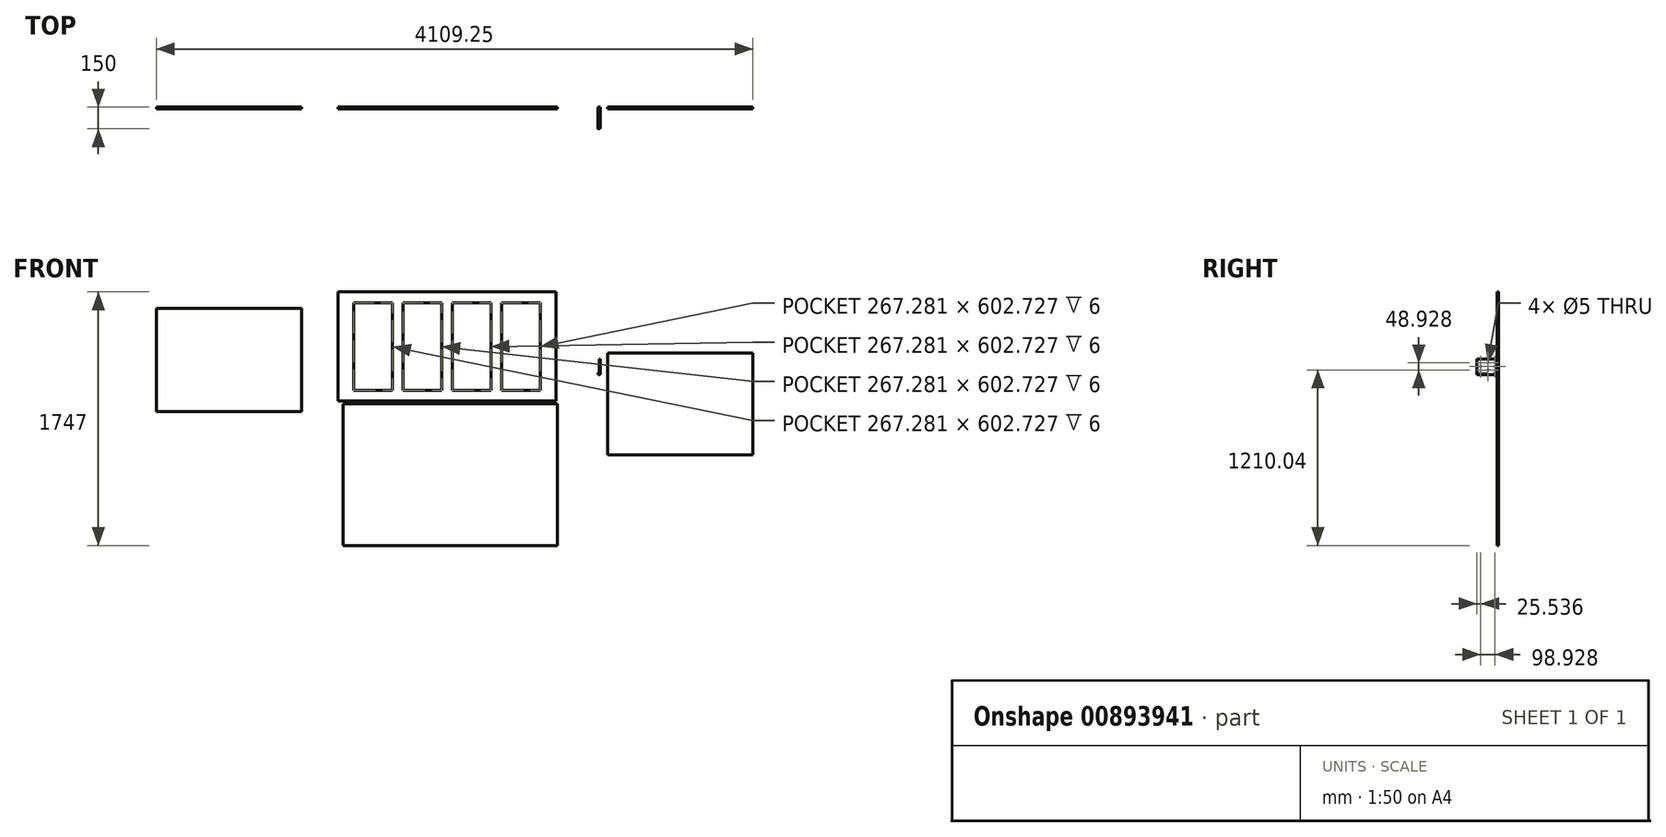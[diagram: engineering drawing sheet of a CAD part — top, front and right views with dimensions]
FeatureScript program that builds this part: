
annotation { "Feature Type Name" : "Feature", "Feature Type Description" : "" }
export const myFeature = defineFeature(function(context is Context, id is Id, definition is map)
    precondition{}
    {
        {
            assignVariable(context, id + "F0", {"name" : "thickness", "anyValue" : 12 * mm});
        }
        {
            var Q0;
            Q0=qCreatedBy(makeId("Front.planeOp"),FACE);
            var sketch = newSketch(context, id + "F1", { "sketchPlane" : qUnion([Q0])});
            skLineSegment(sketch, "E0.bottom", {"start": v(-755.12, 365.58) * mm, "end": v(744.88, 365.58) * mm});
            skLineSegment(sketch, "E0.top", {"start": v(-755.12, -384.42) * mm, "end": v(744.88, -384.42) * mm});
            skLineSegment(sketch, "E0.left", {"start": v(-755.12, 365.58) * mm, "end": v(-755.12, -384.42) * mm});
            skLineSegment(sketch, "E0.right", {"start": v(744.88, 365.58) * mm, "end": v(744.88, -384.42) * mm});
            skSolve(sketch);
        }
        {
            var Q0;
            Q0=makeQuery(id+"F1.imprint","IMPRINT",FACE,{"disambiguationData":[TD([[makeQuery(id+"F1.imprint","IMPRINT",EDGE,{"derivedFrom":sQuery(id+"F1.wireOp",EDGE,"E0.bottom")}),-1.0]])]});
            extrude(context, id + "F2", {"entities" : qUnion([Q0]), "depth" : getVariable(context, 'thickness'), "offsetDistance" : 25 * mm});
        }
        {
            var Q0;
            Q0=makeQuery(id+"F2.opExtrude","CAP_FACE",FACE,{"disambiguationData":[OSD([sQuery(id+"F1.wireOp",EDGE,"E0.bottom"),sQuery(id+"F1.wireOp",EDGE,"E0.top"),sQuery(id+"F1.wireOp",EDGE,"E0.left"),sQuery(id+"F1.wireOp",EDGE,"E0.right")])],"isStart":false});
            var sketch = newSketch(context, id + "F3", { "sketchPlane" : qUnion([Q0])});
            skLineSegment(sketch, "E1.bottom", {"start": v(-647.31, 291.94) * mm, "end": v(-380.03, 291.94) * mm});
            skLineSegment(sketch, "E1.top", {"start": v(-647.31, -310.78) * mm, "end": v(-380.03, -310.78) * mm});
            skLineSegment(sketch, "E1.left", {"start": v(-647.31, 291.94) * mm, "end": v(-647.31, -310.78) * mm});
            skLineSegment(sketch, "E1.right", {"start": v(-380.03, 291.94) * mm, "end": v(-380.03, -310.78) * mm});
            skLineSegment(sketch, "E2.bottom", {"start": v(-308.27, 291.94) * mm, "end": v(-41, 291.94) * mm});
            skLineSegment(sketch, "E2.top", {"start": v(-308.27, -310.78) * mm, "end": v(-41, -310.78) * mm});
            skLineSegment(sketch, "E2.left", {"start": v(-308.27, 291.94) * mm, "end": v(-308.27, -310.78) * mm});
            skLineSegment(sketch, "E2.right", {"start": v(-41, 291.94) * mm, "end": v(-41, -310.78) * mm});
            skLineSegment(sketch, "E3.bottom", {"start": v(30.76, -310.78) * mm, "end": v(298.04, -310.78) * mm});
            skLineSegment(sketch, "E3.top", {"start": v(30.76, 291.94) * mm, "end": v(298.04, 291.94) * mm});
            skLineSegment(sketch, "E3.left", {"start": v(30.76, -310.78) * mm, "end": v(30.76, 291.94) * mm});
            skLineSegment(sketch, "E3.right", {"start": v(298.04, -310.78) * mm, "end": v(298.04, 291.94) * mm});
            skLineSegment(sketch, "E4.bottom", {"start": v(369.8, -310.78) * mm, "end": v(637.08, -310.78) * mm});
            skLineSegment(sketch, "E4.top", {"start": v(369.8, 291.94) * mm, "end": v(637.08, 291.94) * mm});
            skLineSegment(sketch, "E4.left", {"start": v(369.8, -310.78) * mm, "end": v(369.8, 291.94) * mm});
            skLineSegment(sketch, "E4.right", {"start": v(637.08, -310.78) * mm, "end": v(637.08, 291.94) * mm});
            skLineSegment(sketch, "E5", {"start": v(-308.27, 291.94) * mm, "end": v(-308.27, 365.58) * mm, "construction": true});
            skLineSegment(sketch, "E6", {"start": v(-308.27, -310.78) * mm, "end": v(-308.27, -384.42) * mm, "construction": true});
            skLineSegment(sketch, "E7", {"start": v(-380.03, 291.94) * mm, "end": v(-380.03, 365.58) * mm, "construction": true});
            skLineSegment(sketch, "E8", {"start": v(-10.67, 291.94) * mm, "end": v(-10.67, 365.58) * mm, "construction": true});
            skLineSegment(sketch, "E9", {"start": v(369.8, 291.94) * mm, "end": v(369.8, 365.58) * mm, "construction": true});
            skLineSegment(sketch, "E10", {"start": v(-380.03, -310.78) * mm, "end": v(-380.03, -384.42) * mm, "construction": true});
            skLineSegment(sketch, "E11", {"start": v(30.76, -310.78) * mm, "end": v(30.76, -384.42) * mm, "construction": true});
            skLineSegment(sketch, "E12", {"start": v(369.8, -384.42) * mm, "end": v(369.8, -310.78) * mm, "construction": true});
            skLineSegment(sketch, "E13", {"start": v(-380.03, 291.94) * mm, "end": v(-308.27, 291.94) * mm, "construction": true});
            skLineSegment(sketch, "E14", {"start": v(-41, 291.94) * mm, "end": v(30.76, 291.94) * mm, "construction": true});
            skLineSegment(sketch, "E15", {"start": v(298.04, 291.94) * mm, "end": v(369.8, 291.94) * mm, "construction": true});
            skLineSegment(sketch, "E16", {"start": v(-647.31, 291.94) * mm, "end": v(-755.12, 291.94) * mm, "construction": true});
            skLineSegment(sketch, "E17", {"start": v(637.08, 291.94) * mm, "end": v(744.88, 291.94) * mm, "construction": true});
            skSolve(sketch);
        }
        {
            var Q0;
            Q0=makeQuery(id+"F3.imprint","IMPRINT",FACE,{"disambiguationData":[TD([[makeQuery(id+"F3.imprint","IMPRINT",EDGE,{"derivedFrom":sQuery(id+"F3.wireOp",EDGE,"E1.bottom")}),-1.0]])]});
            var Q1;
            Q1=makeQuery(id+"F3.imprint","IMPRINT",FACE,{"disambiguationData":[TD([[makeQuery(id+"F3.imprint","IMPRINT",EDGE,{"derivedFrom":sQuery(id+"F3.wireOp",EDGE,"E2.bottom")}),-1.0]])]});
            var Q2;
            Q2=makeQuery(id+"F3.imprint","IMPRINT",FACE,{"disambiguationData":[TD([[makeQuery(id+"F3.imprint","IMPRINT",EDGE,{"derivedFrom":sQuery(id+"F3.wireOp",EDGE,"E3.bottom")}),1.0]])]});
            var Q3;
            Q3=makeQuery(id+"F3.imprint","IMPRINT",FACE,{"disambiguationData":[TD([[makeQuery(id+"F3.imprint","IMPRINT",EDGE,{"derivedFrom":sQuery(id+"F3.wireOp",EDGE,"E4.bottom")}),1.0]])]});
            extrude(context, id + "F4", {"entities" : qUnion([Q0, Q1, Q2, Q3]), "operationType" : NewBodyOperationType.REMOVE, "oppositeDirection" : true, "depth" : getVariable(context, 'thickness') / 2, "offsetDistance" : 25 * mm});
        }
        {
            var Q0;
            Q0=qCreatedBy(makeId("Front.planeOp"),FACE);
            var sketch = newSketch(context, id + "F5", { "sketchPlane" : qUnion([Q0])});
            skCircle(sketch, "E18", {"center": v(1043.1, -196.91) * mm, "radius": 7.5 * mm});
            skLineSegment(sketch, "E19", {"start": v(1045.6, -189.84) * mm, "end": v(1045.6, -96.91) * mm});
            skLineSegment(sketch, "E20", {"start": v(1045.6, -96.91) * mm, "end": v(1050.6, -96.91) * mm});
            skLineSegment(sketch, "E21", {"start": v(1050.6, -96.91) * mm, "end": v(1050.6, -196.91) * mm});
            skPoint(sketch, "E22", {"position": v(1048.1, -96.91) * mm});
            skSolve(sketch);
        }
        {
            var Q0;
            {var subQ0=sQuery(id+"F5.wireOp",EDGE,"E19");Q0=makeQuery(id+"F5.imprint","IMPRINT",FACE,{"disambiguationData":[TD([[makeQuery(id+"F5.imprint","IMPRINT",EDGE,{"derivedFrom":subQ0}),-1.0]])]});}
            var Q1;
            {var subQ0=sQuery(id+"F5.wireOp",EDGE,"E18");var subQ1=makeQuery(id+"F5.imprint","INTERSECT",VERTEX,{"derivedFrom":[subQ0,sQuery(id+"F5.wireOp",EDGE,"E19")]});Q1=makeQuery(id+"F5.imprint","IMPRINT",FACE,{"disambiguationData":[TD([[makeQuery(id+"F5.imprint","IMPRINT",EDGE,{"disambiguationData":[TD([[subQ1,1.0]])],"derivedFrom":subQ0}),1.0]])]});}
            extrude(context, id + "F6", {"entities" : qUnion([Q0, Q1]), "depth" : 150 * mm, "offsetDistance" : 25 * mm});
        }
        {
            var Q0;
            Q0=makeQuery(id+"F6.opExtrude","SWEPT_FACE",FACE,{"disambiguationData":[OSD([sQuery(id+"F5.wireOp",EDGE,"E21")])]});
            var sketch = newSketch(context, id + "F7", { "sketchPlane" : qUnion([Q0])});
            skPoint(sketch, "E23", {"position": v(-150, -146.91) * mm});
            skPoint(sketch, "E24", {"position": v(0, -146.91) * mm});
            skCircle(sketch, "E25", {"center": v(-124.46, -146.91) * mm, "radius": 2.5 * mm});
            skCircle(sketch, "E26", {"center": v(-25.54, -146.91) * mm, "radius": 2.5 * mm});
            skCircle(sketch, "E27", {"center": v(-75, -122.45) * mm, "radius": 2.5 * mm});
            skCircle(sketch, "E28", {"center": v(-75, -171.38) * mm, "radius": 2.5 * mm});
            skPoint(sketch, "E29", {"position": v(-75, -96.91) * mm});
            skLineSegment(sketch, "E30", {"start": v(-124.46, -146.91) * mm, "end": v(-150, -146.91) * mm, "construction": true});
            skLineSegment(sketch, "E31", {"start": v(-75, -122.45) * mm, "end": v(-75, -96.91) * mm, "construction": true});
            skLineSegment(sketch, "E32", {"start": v(-25.54, -146.91) * mm, "end": v(0, -146.91) * mm, "construction": true});
            skLineSegment(sketch, "E33", {"start": v(-75, -171.38) * mm, "end": v(-75, -196.91) * mm, "construction": true});
            skSolve(sketch);
        }
        {
            var Q0;
            Q0=makeQuery(id+"F7.imprint","IMPRINT",FACE,{"disambiguationData":[TD([[makeQuery(id+"F7.imprint","IMPRINT",EDGE,{"derivedFrom":sQuery(id+"F7.wireOp",EDGE,"E25")}),1.0]])]});
            var Q1;
            Q1=makeQuery(id+"F7.imprint","IMPRINT",FACE,{"disambiguationData":[TD([[makeQuery(id+"F7.imprint","IMPRINT",EDGE,{"derivedFrom":sQuery(id+"F7.wireOp",EDGE,"E27")}),1.0]])]});
            var Q2;
            Q2=makeQuery(id+"F7.imprint","IMPRINT",FACE,{"disambiguationData":[TD([[makeQuery(id+"F7.imprint","IMPRINT",EDGE,{"derivedFrom":sQuery(id+"F7.wireOp",EDGE,"E28")}),1.0]])]});
            var Q3;
            Q3=makeQuery(id+"F7.imprint","IMPRINT",FACE,{"disambiguationData":[TD([[makeQuery(id+"F7.imprint","IMPRINT",EDGE,{"derivedFrom":sQuery(id+"F7.wireOp",EDGE,"E26")}),1.0]])]});
            extrude(context, id + "F8", {"entities" : qUnion([Q0, Q1, Q2, Q3]), "operationType" : NewBodyOperationType.REMOVE, "endBound" : BoundingType.UP_TO_NEXT, "oppositeDirection" : true, "depth" : 25 * mm, "offsetDistance" : 25 * mm});
        }
        {
            var Q0;
            Q0=qCreatedBy(makeId("Front.planeOp"),FACE);
            var sketch = newSketch(context, id + "F9", { "sketchPlane" : qUnion([Q0])});
            skLineSegment(sketch, "E34.bottom", {"start": v(-1007.6, 254.04) * mm, "end": v(-2007.6, 254.04) * mm});
            skLineSegment(sketch, "E34.top", {"start": v(-1007.6, -459.96) * mm, "end": v(-2007.6, -459.96) * mm});
            skLineSegment(sketch, "E34.left", {"start": v(-1007.6, 254.04) * mm, "end": v(-1007.6, -459.96) * mm});
            skLineSegment(sketch, "E34.right", {"start": v(-2007.6, 254.04) * mm, "end": v(-2007.6, -459.96) * mm});
            skSolve(sketch);
        }
        {
            var Q0;
            Q0=makeQuery(id+"F9.imprint","IMPRINT",FACE,{"disambiguationData":[TD([[makeQuery(id+"F9.imprint","IMPRINT",EDGE,{"derivedFrom":sQuery(id+"F9.wireOp",EDGE,"E34.bottom")}),1.0]])]});
            extrude(context, id + "F10", {"entities" : qUnion([Q0]), "depth" : getVariable(context, 'thickness'), "offsetDistance" : 25 * mm});
        }
        {
            var Q0;
            Q0=qCreatedBy(makeId("Front.planeOp"),FACE);
            var sketch = newSketch(context, id + "F11", { "sketchPlane" : qUnion([Q0])});
            skLineSegment(sketch, "E35.bottom", {"start": v(1101.65, -54.65) * mm, "end": v(2101.65, -54.65) * mm});
            skLineSegment(sketch, "E35.top", {"start": v(1101.65, -756.65) * mm, "end": v(2101.65, -756.65) * mm});
            skLineSegment(sketch, "E35.left", {"start": v(1101.65, -54.65) * mm, "end": v(1101.65, -756.65) * mm});
            skLineSegment(sketch, "E35.right", {"start": v(2101.65, -54.65) * mm, "end": v(2101.65, -756.65) * mm});
            skSolve(sketch);
        }
        {
            var Q0;
            Q0=makeQuery(id+"F11.imprint","IMPRINT",FACE,{"disambiguationData":[TD([[makeQuery(id+"F11.imprint","IMPRINT",EDGE,{"derivedFrom":sQuery(id+"F11.wireOp",EDGE,"E35.bottom")}),-1.0]])]});
            extrude(context, id + "F12", {"entities" : qUnion([Q0]), "depth" : getVariable(context, 'thickness'), "offsetDistance" : 25 * mm});
        }
        {
            var Q0;
            Q0=qCreatedBy(makeId("Front.planeOp"),FACE);
            var sketch = newSketch(context, id + "F13", { "sketchPlane" : qUnion([Q0])});
            skLineSegment(sketch, "E36.bottom", {"start": v(-720.9, -405.42) * mm, "end": v(755.1, -405.42) * mm});
            skLineSegment(sketch, "E36.top", {"start": v(-720.9, -1381.42) * mm, "end": v(755.1, -1381.42) * mm});
            skLineSegment(sketch, "E36.left", {"start": v(-720.9, -405.42) * mm, "end": v(-720.9, -1381.42) * mm});
            skLineSegment(sketch, "E36.right", {"start": v(755.1, -405.42) * mm, "end": v(755.1, -1381.42) * mm});
            skSolve(sketch);
        }
        {
            var Q0;
            Q0=makeQuery(id+"F13.imprint","IMPRINT",FACE,{"disambiguationData":[TD([[makeQuery(id+"F13.imprint","IMPRINT",EDGE,{"derivedFrom":sQuery(id+"F13.wireOp",EDGE,"E36.bottom")}),-1.0]])]});
            extrude(context, id + "F14", {"entities" : qUnion([Q0]), "depth" : getVariable(context, 'thickness'), "offsetDistance" : 25 * mm});
        }
    });
